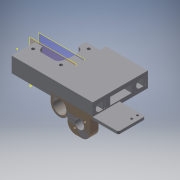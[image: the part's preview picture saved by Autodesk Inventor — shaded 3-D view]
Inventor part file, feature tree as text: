
AUTODESK INVENTOR PART (.ipt)
format: ipt  version: 2016 (Build 200138000, 138)  size: 3,011,072 bytes
history: native  units: mm
features: sketch x9, extrude x6, other x5, projected_geometry x5, hole x2, plane x2, direct_edit x1, mirror x1, imported_body x1, move_body x1
ambient origin geometry x8: Origin, YZ Plane, XZ Plane, XY Plane, X Axis, Y Axis, Z Axis, Center Point
bodies: Solid1 (feature_tree), Solid2 (feature_tree)
feature tree (33):
  other  "z_right_printer_1"
  other  "MeshFeature1"
  direct_edit  "Direct Edit1"
  sketch  "Sketch1"  dims[d0=0.0mm d1=0.0mm d2=5.5mm]
  other  "Work Point1"
  hole  "Hole1"  [1 undecoded]
  extrude  "Extrusion1"  Depth=16.0mm
  hole  "Hole2"  [1 undecoded]
  sketch  "Sketch5"  dims[d14=3.2mm d15=6.0mm d16=4.0mm d17=2.0mm d18=90.0deg d19=23.5mm d20=20.594885mm d21=1.0mm]
  extrude  "Extrusion2"  Depth=1.0mm TaperAngle=0.0deg
  extrude  "Extrusion3"  [1 undecoded]
  plane  "Work Plane1"
  plane  "Work Plane2"
  extrude  "Extrusion4"  Depth=27.0mm TaperAngle=0.0deg
  mirror  "Mirror1"
  extrude  "Extrusion5"  [1 undecoded]
  extrude  "Extrusion6"  [1 undecoded]
  imported_body  "Base2"
  projected_geometry  "Projected Loop1"
  sketch  "Sketch3"  dims[d3=10.5mm d4=6.0mm d5=4.0mm d6=2.0mm d7=90.0deg d8=8.0mm d9=20.594885mm d10=16.0mm]
  projected_geometry  "Projected Loop3"
  sketch  "Sketch4"  dims[d11=10.0mm d12=0.0mm d13=16.0mm]
  sketch  "Sketch6"  dims[d22=1.0mm d23=0.0mm d24=1.0mm d25=0.0mm]
  sketch  "Sketch7"  dims[d26=-26.0mm d27=-26.0mm]
  projected_geometry  "Projected Loop5"
  projected_geometry  "Projected Loop6"
  sketch  "Sketch8"  dims[d28=7.5mm d29=0.0mm d30=27.0mm d31=0.0mm]
  projected_geometry  "Projected Loop7"
  sketch  "Sketch9"  dims[d32=16.0mm d33=0.0mm]
  sketch  "Sketch10"
  other  "Composite1"
  move_body  "Move1"
  other  "Srf1"
note: 5 required parameter values undecoded (feature->parameter linkage not recoverable at this tier; creation-order binding heuristic only, values carry confidence <= 0.55)
